# Revit family: Drinking_Fountain-Haws_Corporation-Pedestal_3377BF
name_source: partatom
category: Plumbing Fixtures
revit_build: Autodesk Revit Architecture 2015 (Build: 20140606_1530(x64)
units: mm (PartAtom-declared; Revit-internal decimal feet)

## types (1)
- 3377BF
    Bowl = Metal - Haws Corporation - Satin Stainless Steel
    Bracket = Metal - Haws Corporation - Satin Stainless Steel
    CW Connection = Yes
    CWFU = 1
    Default Elevation = 4' - 0"
    Description = Pedestal fountain utilizes a satin finish stainless steel bracket, 100% lead-free waterways, laminar flow, and painted galvanized steel pedestal extension.
    HW Connection = No
    HWFU = 0
    Height = 4' - 0"
    Manufacturer = Haws Corporation
    Model = 3377BF on 3377
    Pedestal = Metal - Haws Corporation - Green Powder Coated Finish
    Product Documentation Link = https://www.hawsco.com
    Product Name = Barrier-Free Steel Pedestal Fountain w/ Bottle Filler Attachment
    Product Page URL = https://www.hawsco.com
    SKU = 10-101
    Sanitary Radius = 0' - 0 5/8"
    Supply Radius = 0' - 0 3/16"
    Trim Plate = No
    Tubing = Metal - Haws Corporation - Copper
    URL = https://www.hawsco.com
    Vent Connection = No
    Version = 2014-v1.0a
    WFU = 1
    Warranty URL = https://www.hawsco.com
    Waste Connection = Yes
    con L = Yes

## geometry (parser evidence)
native form markers: Blend x16, Sweep x5
no freeform markers — native parametric forms only
